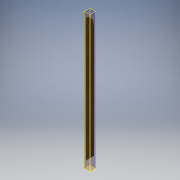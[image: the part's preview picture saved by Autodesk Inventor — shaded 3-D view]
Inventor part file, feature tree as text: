
AUTODESK INVENTOR PART (.ipt)
format: ipt  version: 2018 (Build 220112000, 112)  size: 114,176 bytes
history: native  units: mm
features: other x7, extrude x1, sketch x1
ambient origin geometry x8: Origin, YZ Plane, XZ Plane, XY Plane, X Axis, Y Axis, Z Axis, Center Point
bodies: Body1 (feature_tree)
feature tree (9):
  other  "ソリッド1"
  extrude  "押し出し1"  Depth=27.2mm
  other  "面の勾配1"
  other  "面の勾配2"
  other  "作業平面1"
  other  "作業平面2"
  other  "作業平面3"
  other  "作業平面4"
  sketch  "スケッチ1"
